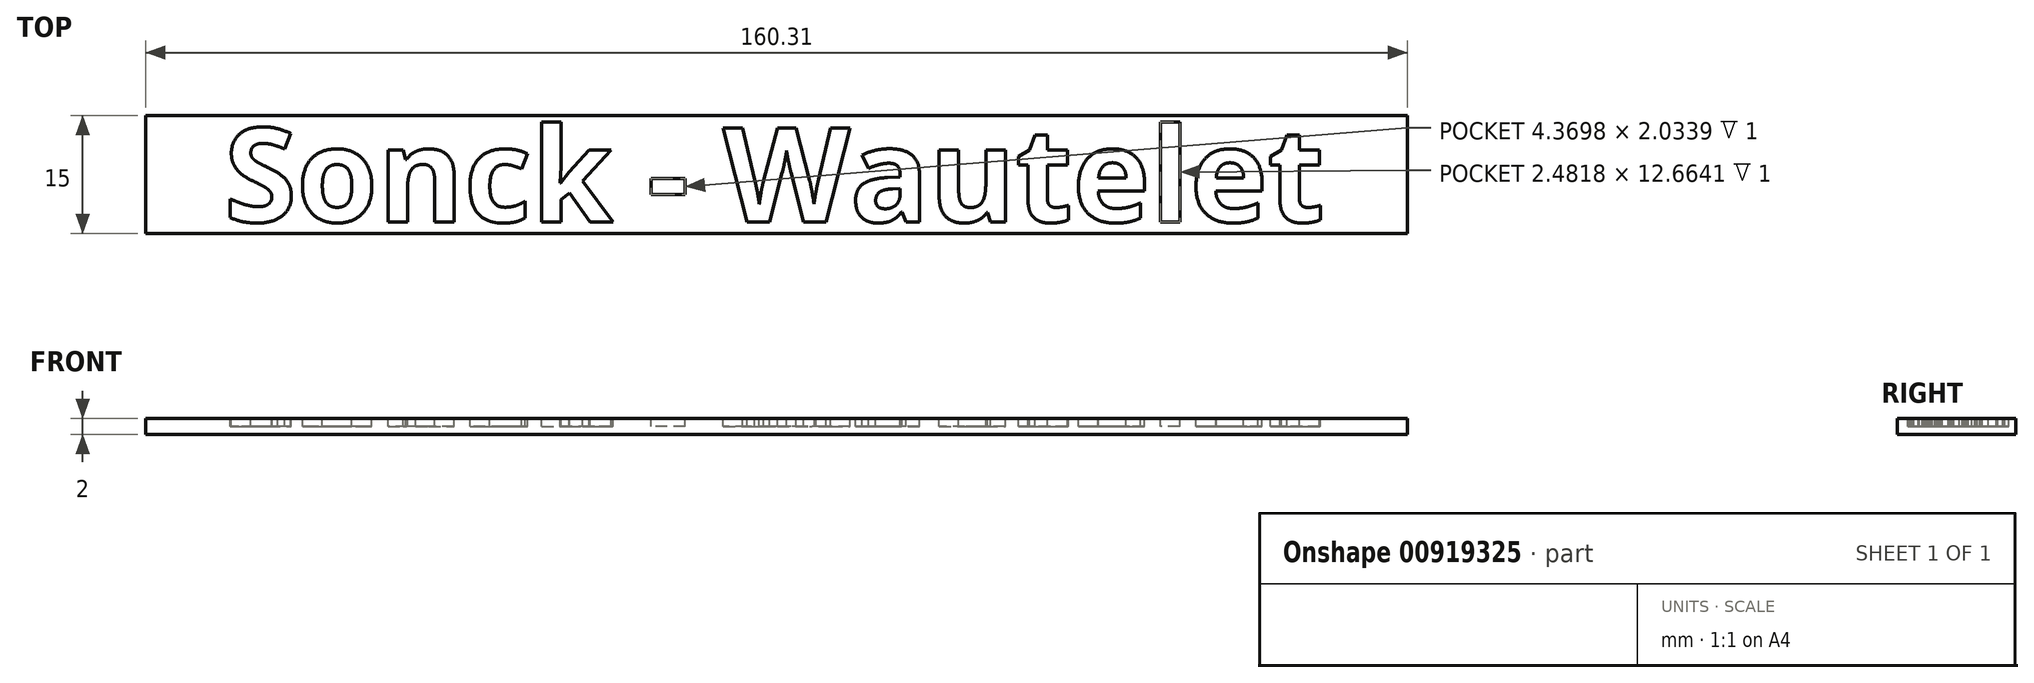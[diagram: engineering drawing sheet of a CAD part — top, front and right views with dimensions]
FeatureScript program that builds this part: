
annotation { "Feature Type Name" : "Feature", "Feature Type Description" : "" }
export const myFeature = defineFeature(function(context is Context, id is Id, definition is map)
    precondition{}
    {
        {
            var Q0;
            Q0=qCreatedBy(makeId("Top.planeOp"),FACE);
            var sketch = newSketch(context, id + "F0", { "sketchPlane" : qUnion([Q0])});
            skLineSegment(sketch, "E0.bottom", {"start": v(-75.31, 7.5) * mm, "end": v(85, 7.5) * mm});
            skLineSegment(sketch, "E0.top", {"start": v(-75.31, -7.5) * mm, "end": v(85, -7.5) * mm});
            skLineSegment(sketch, "E0.left", {"start": v(-75.31, 7.5) * mm, "end": v(-75.31, -7.5) * mm});
            skLineSegment(sketch, "E0.right", {"start": v(85, 7.5) * mm, "end": v(85, -7.5) * mm});
            skSolve(sketch);
        }
        {
            var Q0;
            Q0=makeQuery(id+"F0.imprint","IMPRINT",FACE,{"disambiguationData":[TD([[makeQuery(id+"F0.imprint","IMPRINT",EDGE,{"derivedFrom":sQuery(id+"F0.wireOp",EDGE,"E0.bottom")}),-1.0]])]});
            extrude(context, id + "F1", {"entities" : qUnion([Q0]), "depth" : 2 * mm, "offsetDistance" : 25 * mm});
        }
        {
            var Q0;
            Q0=makeQuery(id+"F1.opExtrude","CAP_FACE",FACE,{"disambiguationData":[OSD([sQuery(id+"F0.wireOp",EDGE,"E0.bottom"),sQuery(id+"F0.wireOp",EDGE,"E0.top"),sQuery(id+"F0.wireOp",EDGE,"E0.left"),sQuery(id+"F0.wireOp",EDGE,"E0.right")])],"isStart":false});
            cPlane(context, id + "F2", {"entities" : qUnion([Q0]), "cplaneType" : CPlaneType.OFFSET, "offset" : 0 * mm, "width" : 150 * mm, "height" : 150 * mm});
        }
        {
            var Q0;
            Q0=qCreatedBy(id+"F2.planeOp",FACE);
            var sketch = newSketch(context, id + "F3", { "sketchPlane" : qUnion([Q0])});
            skText(sketch, "E1", { "text": "Sonck - Wautelet", "fontName": "OpenSans-Bold.ttf"});
            const initialGuessF3  = {"E1": [-0.06531, -0.006, 1, 0, 0.012]};
            skSetInitialGuess(sketch, initialGuessF3);
            skSolve(sketch);
        }
        {
            var Q0;
            Q0 = qSketchRegion(id + "F3", true);
            extrude(context, id + "F4", {"entities" : qUnion([Q0]), "operationType" : NewBodyOperationType.REMOVE, "oppositeDirection" : true, "depth" : 1 * mm, "offsetDistance" : 25 * mm});
        }
    });
